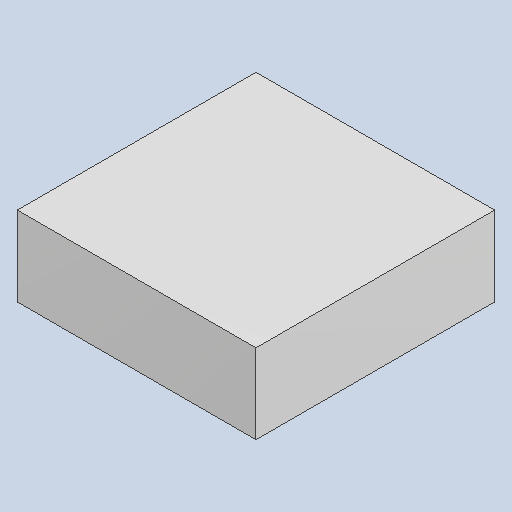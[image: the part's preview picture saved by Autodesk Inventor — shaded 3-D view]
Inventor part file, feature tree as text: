
AUTODESK INVENTOR PART (.ipt)
format: ipt  version: 2023.4 (Build 274418000, 418)  size: 79,872 bytes
history: native  units: mm
features: extrude x1
ambient origin geometry x8: Origin, YZ Plane, XZ Plane, XY Plane, X Axis, Y Axis, Z Axis, Center Point
bodies: Solid1 (feature_tree)
feature tree (1):
  extrude  "Extruded_60"  [1 undecoded]
note: 1 required parameter value undecoded (feature->parameter linkage not recoverable at this tier; creation-order binding heuristic only, values carry confidence <= 0.55)
